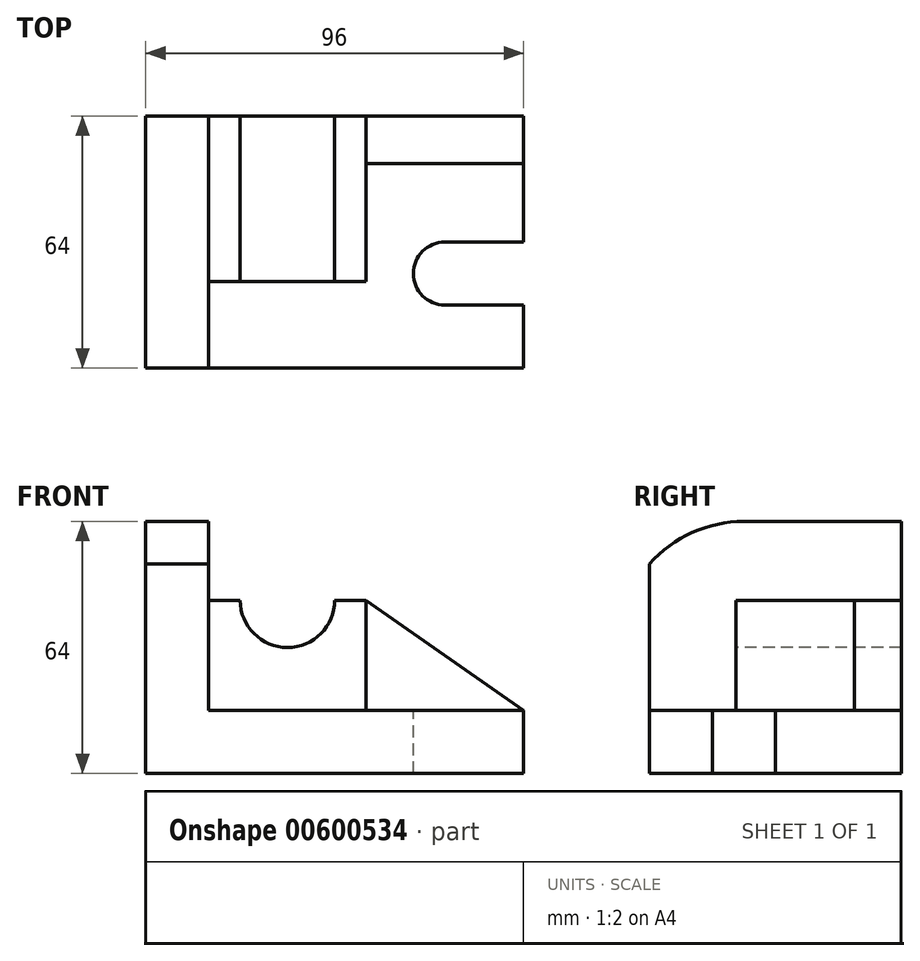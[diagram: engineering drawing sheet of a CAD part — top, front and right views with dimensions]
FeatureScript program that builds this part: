
annotation { "Feature Type Name" : "Feature", "Feature Type Description" : "" }
export const myFeature = defineFeature(function(context is Context, id is Id, definition is map)
    precondition{}
    {
        {
            var Q0;
            Q0=qCreatedBy(makeId("Top.planeOp"),FACE);
            var sketch = newSketch(context, id + "F0", { "sketchPlane" : qUnion([Q0])});
            skLineSegment(sketch, "E0.bottom", {"start": v(-89.83, 24) * mm, "end": v(6.17, 24) * mm});
            skLineSegment(sketch, "E0.top", {"start": v(-89.83, -40) * mm, "end": v(6.17, -40) * mm});
            skLineSegment(sketch, "E0.left", {"start": v(-89.83, 24) * mm, "end": v(-89.83, -40) * mm});
            skLineSegment(sketch, "E0.right", {"start": v(6.17, 24) * mm, "end": v(6.17, -40) * mm});
            skSolve(sketch);
        }
        {
            var Q0;
            Q0 = qSketchRegion(id + "F0", true);
            extrude(context, id + "F1", {"entities" : qUnion([Q0]), "depth" : 16 * mm, "offsetDistance" : 25 * mm});
        }
        {
            var Q0;
            Q0=makeQuery(id+"F1.opExtrude","SWEPT_FACE",FACE,{"disambiguationData":[OSD([sQuery(id+"F0.wireOp",EDGE,"E0.left")])]});
            var sketch = newSketch(context, id + "F2", { "sketchPlane" : qUnion([Q0])});
            skLineSegment(sketch, "E1", {"start": v(-24, 16) * mm, "end": v(-24, 64) * mm});
            skLineSegment(sketch, "E2", {"start": v(-24, 64) * mm, "end": v(16.01, 64) * mm});
            skLineSegment(sketch, "E3", {"start": v(-24, 16) * mm, "end": v(40, 16) * mm});
            skLineSegment(sketch, "E4", {"start": v(40, 16) * mm, "end": v(40, 53.2) * mm});
            skArc(sketch, "E5", {"start": v(16.01, 64) * mm, "mid": v(29.17, 61.17) * mm, "end": v(40, 53.2) * mm});
            skSolve(sketch);
        }
        {
            var Q0;
            Q0=makeQuery(id+"F2.imprint","IMPRINT",FACE,{"disambiguationData":[TD([[makeQuery(id+"F2.imprint","IMPRINT",EDGE,{"derivedFrom":sQuery(id+"F2.wireOp",EDGE,"E1")}),-1.0]])]});
            extrude(context, id + "F3", {"entities" : qUnion([Q0]), "operationType" : NewBodyOperationType.ADD, "oppositeDirection" : true, "depth" : 16 * mm, "offsetDistance" : 25 * mm});
        }
        {
            var Q0;
            Q0=makeQuery(id+"F3.boolean.opBoolean","MERGE",FACE,{"derivedFrom":[makeQuery(id+"F1.opExtrude","SWEPT_FACE",FACE,{"disambiguationData":[OSD([sQuery(id+"F0.wireOp",EDGE,"E0.bottom")])]}),makeQuery(id+"F3.opExtrude","SWEPT_FACE",FACE,{"disambiguationData":[OSD([sQuery(id+"F2.wireOp",EDGE,"E1")])]})]});
            var sketch = newSketch(context, id + "F4", { "sketchPlane" : qUnion([Q0])});
            skLineSegment(sketch, "E6.bottom", {"start": v(73.83, 16) * mm, "end": v(33.83, 16) * mm});
            skLineSegment(sketch, "E6.top", {"start": v(73.83, 44) * mm, "end": v(33.83, 44) * mm});
            skLineSegment(sketch, "E6.left", {"start": v(73.83, 16) * mm, "end": v(73.83, 44) * mm});
            skLineSegment(sketch, "E6.right", {"start": v(33.83, 16) * mm, "end": v(33.83, 44) * mm});
            skSolve(sketch);
        }
        {
            var Q0;
            Q0=makeQuery(id+"F4.imprint","IMPRINT",FACE,{"disambiguationData":[TD([[makeQuery(id+"F4.imprint","IMPRINT",EDGE,{"derivedFrom":sQuery(id+"F4.wireOp",EDGE,"E6.bottom")}),-1.0]])]});
            extrude(context, id + "F5", {"entities" : qUnion([Q0]), "operationType" : NewBodyOperationType.ADD, "oppositeDirection" : true, "depth" : 42 * mm, "offsetDistance" : 25 * mm});
        }
        {
            var Q0;
            Q0=makeQuery(id+"F5.opExtrude","CAP_FACE",FACE,{"disambiguationData":[OSD([sQuery(id+"F4.wireOp",EDGE,"E6.bottom"),sQuery(id+"F4.wireOp",EDGE,"E6.top"),sQuery(id+"F4.wireOp",EDGE,"E6.left"),sQuery(id+"F4.wireOp",EDGE,"E6.right")])],"isStart":false});
            var sketch = newSketch(context, id + "F6", { "sketchPlane" : qUnion([Q0])});
            skArc(sketch, "E7", {"start": v(-41.83, 44) * mm, "mid": v(-53.83, 32) * mm, "end": v(-65.83, 44) * mm});
            skLineSegment(sketch, "E8", {"start": v(-41.83, 44) * mm, "end": v(-65.83, 44) * mm});
            skSolve(sketch);
        }
        {
            var Q0;
            Q0 = qSketchRegion(id + "F6", true);
            extrude(context, id + "F7", {"entities" : qUnion([Q0]), "operationType" : NewBodyOperationType.REMOVE, "oppositeDirection" : true, "depth" : 42 * mm, "offsetDistance" : 25 * mm});
        }
        {
            var Q0;
            Q0=makeQuery(id+"F1.opExtrude","CAP_FACE",FACE,{"disambiguationData":[OSD([sQuery(id+"F0.wireOp",EDGE,"E0.bottom"),sQuery(id+"F0.wireOp",EDGE,"E0.top"),sQuery(id+"F0.wireOp",EDGE,"E0.left"),sQuery(id+"F0.wireOp",EDGE,"E0.right")])],"isStart":false});
            var sketch = newSketch(context, id + "F8", { "sketchPlane" : qUnion([Q0])});
            skLineSegment(sketch, "E9.bottom", {"start": v(6.17, -24) * mm, "end": v(-13.83, -24) * mm});
            skLineSegment(sketch, "E9.top", {"start": v(6.17, -8) * mm, "end": v(-13.83, -8) * mm});
            skLineSegment(sketch, "E9.left", {"start": v(6.17, -24) * mm, "end": v(6.17, -8) * mm});
            skLineSegment(sketch, "E9.right", {"start": v(-13.83, -24) * mm, "end": v(-13.83, -8) * mm});
            skArc(sketch, "E10", {"start": v(-13.83, -24) * mm, "mid": v(-21.83, -16) * mm, "end": v(-13.83, -8) * mm});
            skSolve(sketch);
        }
        {
            var Q0;
            Q0 = qSketchRegion(id + "F8", true);
            extrude(context, id + "F9", {"entities" : qUnion([Q0]), "operationType" : NewBodyOperationType.REMOVE, "oppositeDirection" : true, "depth" : 16 * mm, "offsetDistance" : 25 * mm});
        }
        {
            var Q0;
            Q0=makeQuery(id+"F5.boolean.opBoolean","MERGE",FACE,{"derivedFrom":[makeQuery(id+"F3.boolean.opBoolean","MERGE",FACE,{"derivedFrom":[makeQuery(id+"F1.opExtrude","SWEPT_FACE",FACE,{"disambiguationData":[OSD([sQuery(id+"F0.wireOp",EDGE,"E0.bottom")])]}),makeQuery(id+"F3.opExtrude","SWEPT_FACE",FACE,{"disambiguationData":[OSD([sQuery(id+"F2.wireOp",EDGE,"E1")])]})]}),makeQuery(id+"F5.opExtrude","CAP_FACE",FACE,{"disambiguationData":[OSD([sQuery(id+"F4.wireOp",EDGE,"E6.bottom"),sQuery(id+"F4.wireOp",EDGE,"E6.top"),sQuery(id+"F4.wireOp",EDGE,"E6.left"),sQuery(id+"F4.wireOp",EDGE,"E6.right")])],"isStart":true})]});
            var sketch = newSketch(context, id + "F10", { "sketchPlane" : qUnion([Q0])});
            skLineSegment(sketch, "E11", {"start": v(-6.17, 16) * mm, "end": v(33.83, 16) * mm});
            skLineSegment(sketch, "E12", {"start": v(33.83, 16) * mm, "end": v(33.83, 44) * mm});
            skLineSegment(sketch, "E13", {"start": v(33.83, 44) * mm, "end": v(-6.17, 16) * mm});
            skSolve(sketch);
        }
        {
            var Q0;
            Q0 = qSketchRegion(id + "F10", true);
            extrude(context, id + "F11", {"entities" : qUnion([Q0]), "operationType" : NewBodyOperationType.ADD, "oppositeDirection" : true, "depth" : 12 * mm, "offsetDistance" : 25 * mm});
        }
    });
